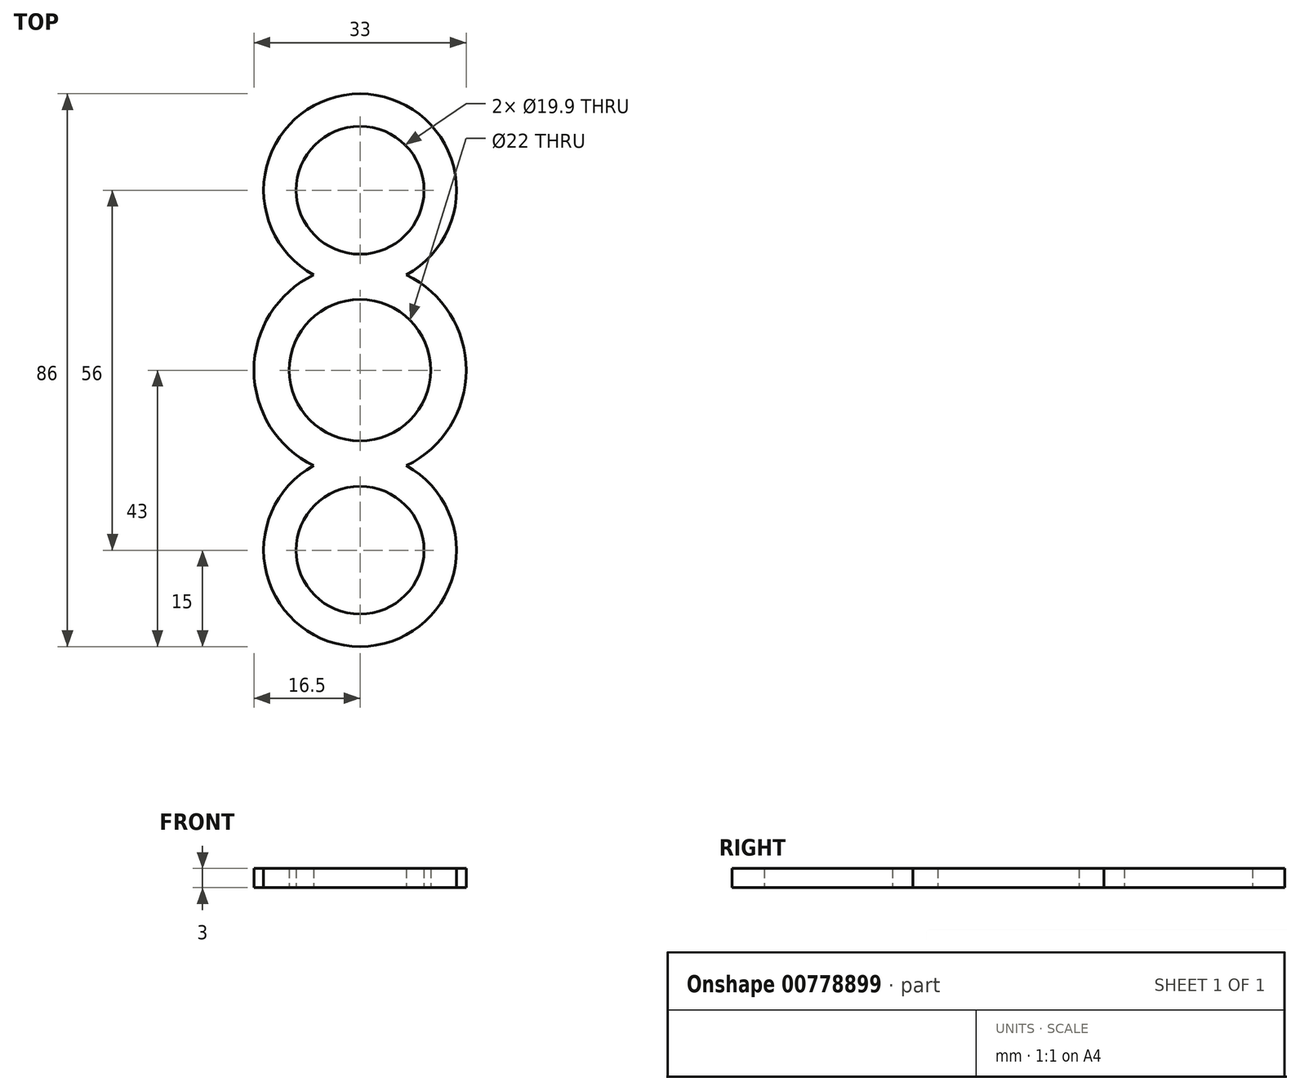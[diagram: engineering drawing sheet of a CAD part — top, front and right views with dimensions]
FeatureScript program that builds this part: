
annotation { "Feature Type Name" : "Feature", "Feature Type Description" : "" }
export const myFeature = defineFeature(function(context is Context, id is Id, definition is map)
    precondition{}
    {
        {
            var Q0;
            Q0=qCreatedBy(makeId("Top.planeOp"),FACE);
            var sketch = newSketch(context, id + "F0", { "sketchPlane" : qUnion([Q0])});
            skCircle(sketch, "E0", {"center": v(0, 0) * mm, "radius": 11 * mm});
            skLineSegment(sketch, "E1", {"start": v(0, 0) * mm, "end": v(0, 28) * mm});
            skCircle(sketch, "E2", {"center": v(0, 28) * mm, "radius": 9.95 * mm});
            skArc(sketch, "E3", {"start": v(-7.2, 14.84) * mm, "mid": v(-16.5, 0) * mm, "end": v(-7.2, -14.84) * mm});
            skArc(sketch, "E4", {"start": v(7.2, 14.84) * mm, "mid": v(0, 43) * mm, "end": v(-7.2, 14.84) * mm});
            skLineSegment(sketch, "E5", {"start": v(0, 0) * mm, "end": v(0, -28) * mm});
            skCircle(sketch, "E6", {"center": v(0, -28) * mm, "radius": 9.95 * mm});
            skArc(sketch, "E7", {"start": v(-7.2, -14.84) * mm, "mid": v(0, -43) * mm, "end": v(7.2, -14.84) * mm});
            skArc(sketch, "E8.trimOffspring", {"start": v(7.2, -14.84) * mm, "mid": v(16.5, 0) * mm, "end": v(7.2, 14.84) * mm});
            skSolve(sketch);
        }
        {
            var Q0;
            Q0=makeQuery(id+"F0.imprint","IMPRINT",FACE,{"disambiguationData":[TD([[makeQuery(id+"F0.imprint","IMPRINT",EDGE,{"derivedFrom":sQuery(id+"F0.wireOp",EDGE,"E2")}),-1.0]])]});
            extrude(context, id + "F1", {"entities" : qUnion([Q0]), "depth" : 3 * mm, "offsetDistance" : 25 * mm});
        }
    });
